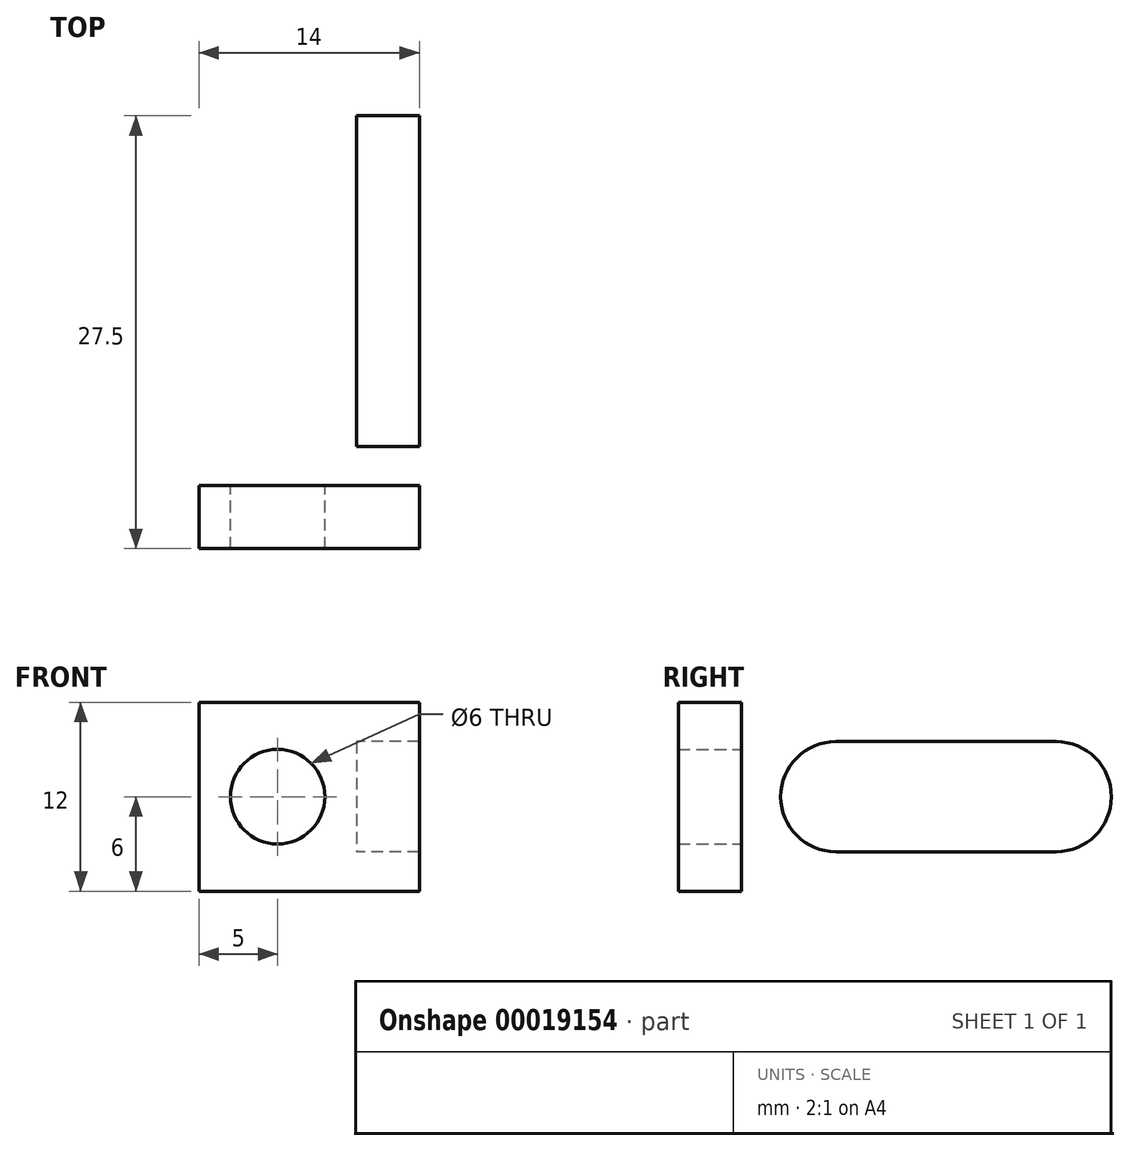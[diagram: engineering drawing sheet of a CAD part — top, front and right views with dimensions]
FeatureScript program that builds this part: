
annotation { "Feature Type Name" : "Feature", "Feature Type Description" : "" }
export const myFeature = defineFeature(function(context is Context, id is Id, definition is map)
    precondition{}
    {
        {
            var Q0;
            Q0=qCreatedBy(makeId("Top.planeOp"),FACE);
            var sketch = newSketch(context, id + "F0", { "sketchPlane" : qUnion([Q0])});
            skLineSegment(sketch, "E0", {"start": v(0, 0) * mm, "end": v(10, 0) * mm});
            skLineSegment(sketch, "E1", {"start": v(10, 0) * mm, "end": v(10, 26) * mm});
            skLineSegment(sketch, "E2", {"start": v(10, 26) * mm, "end": v(14, 26) * mm});
            skLineSegment(sketch, "E3", {"start": v(14, 26) * mm, "end": v(14, -4) * mm});
            skLineSegment(sketch, "E4", {"start": v(14, -4) * mm, "end": v(0, -4) * mm});
            skLineSegment(sketch, "E5", {"start": v(0, -4) * mm, "end": v(0, 0) * mm});
            skSolve(sketch);
        }
        {
            var Q0;
            Q0=makeQuery(id+"F0.imprint","IMPRINT",FACE,{"disambiguationData":[TD([[makeQuery(id+"F0.imprint","IMPRINT",EDGE,{"derivedFrom":sQuery(id+"F0.wireOp",EDGE,"E0")}),-1.0]])]});
            extrude(context, id + "F1", {"entities" : qUnion([Q0]), "depth" : 12 * mm});
        }
        {
            var Q0;
            Q0=makeQuery(id+"F1.opExtrude","SWEPT_FACE",FACE,{"disambiguationData":[OSD([sQuery(id+"F0.wireOp",EDGE,"E1")])]});
            var sketch = newSketch(context, id + "F2", { "sketchPlane" : qUnion([Q0])});
            skLineSegment(sketch, "E6", {"start": v(-20, 6) * mm, "end": v(-6, 6) * mm});
            skPoint(sketch, "E6.startSnap0", {"position": v(-26, 6) * mm});
            skArc(sketch, "E7.0.startCap", {"start": v(-20, 2.5) * mm, "mid": v(-23.5, 6) * mm, "end": v(-20, 9.5) * mm});
            skArc(sketch, "E7.0.endCap", {"start": v(-6, 9.5) * mm, "mid": v(-2.5, 6) * mm, "end": v(-6, 2.5) * mm});
            skLineSegment(sketch, "E7.0.left", {"start": v(-20, 9.5) * mm, "end": v(-6, 9.5) * mm});
            skLineSegment(sketch, "E7.0.right", {"start": v(-20, 2.5) * mm, "end": v(-6, 2.5) * mm});
            skSolve(sketch);
        }
        {
            var Q0;
            Q0=makeQuery(id+"F2.imprint","IMPRINT",FACE,{"disambiguationData":[TD([[makeQuery(id+"F2.imprint","IMPRINT",EDGE,{"derivedFrom":sQuery(id+"F2.wireOp",EDGE,"E7.0.startCap")}),-1.0]])]});
            extrude(context, id + "F3", {"entities" : qUnion([Q0]), "operationType" : NewBodyOperationType.REMOVE, "endBound" : BoundingType.THROUGH_ALL, "oppositeDirection" : true, "depth" : 25 * mm});
        }
        {
            var Q0;
            Q0=makeQuery(id+"F1.opExtrude","SWEPT_FACE",FACE,{"disambiguationData":[OSD([sQuery(id+"F0.wireOp",EDGE,"E0")])]});
            var sketch = newSketch(context, id + "F4", { "sketchPlane" : qUnion([Q0])});
            skLineSegment(sketch, "E8.0.0", {"start": v(-10, 0) * mm, "end": v(0, 0) * mm});
            skLineSegment(sketch, "E8.0.1", {"start": v(0, 0) * mm, "end": v(0, 12) * mm});
            skLineSegment(sketch, "E8.0.2", {"start": v(0, 12) * mm, "end": v(-10, 12) * mm});
            skLineSegment(sketch, "E8.0.3", {"start": v(-10, 12) * mm, "end": v(-10, 0) * mm});
            skCircle(sketch, "E9", {"center": v(-5, 6) * mm, "radius": 3 * mm});
            skPoint(sketch, "E9.centerSnap0", {"position": v(-5, 12) * mm});
            skPoint(sketch, "E9.centerSnap1", {"position": v(0, 6) * mm});
            skSolve(sketch);
        }
        {
            var Q0;
            Q0=makeQuery(id+"F4.imprint","IMPRINT",FACE,{"disambiguationData":[TD([[makeQuery(id+"F4.imprint","IMPRINT",EDGE,{"derivedFrom":sQuery(id+"F4.wireOp",EDGE,"E9")}),1.0]])]});
            extrude(context, id + "F5", {"entities" : qUnion([Q0]), "operationType" : NewBodyOperationType.REMOVE, "endBound" : BoundingType.THROUGH_ALL, "oppositeDirection" : true, "depth" : 25 * mm});
        }
    });
